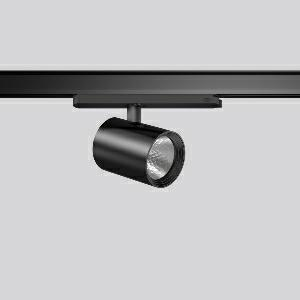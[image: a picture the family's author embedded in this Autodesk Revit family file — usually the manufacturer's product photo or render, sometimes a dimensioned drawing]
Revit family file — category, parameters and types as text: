
# Revit family: deecos_s_mini_track-in_742250_003_2_76_301b
name_source: partatom
category: Lighting Fixtures
units: mm (PartAtom-declared; Revit-internal decimal feet)

## family parameters
Cut with Voids When Loaded = No
Host = Face
Light Source = No
Part Type = Normal
Room Calculation Point = No
Round Connector Dimension = Use Diameter
Shared = No

## types (1)
- DEECOS S mini track-in (1 x LED Modul 927, 2400 lm, 2700)
    Apparent Load = 20 VA
    Approval mark = CE
    CIE Flux Codes = 100 100 100 100 100
    Color Rendering = 92
    Color Temperature = 2700
    Default Elevation = 1800 mm
    Description = Series: DEECOS S mini track-in
LED surface-mounted projector in modern design with no visible cooling ribs. Housing: die-cast aluminium, powder-coated. Rotation range: 356°. Swivel range: 90°. Black plastic ring and recessed LED to prevent glare from the side. Optical assembly with reflector made of MIRO-Silver with 98% total light reflection for outstanding efficiency - can be changed without tools. Best colour rendering index Ra>90. With adapter for RZB 3-circuit DALI tracks. Suitable for Track on ceiling, Wall track. Track-in driver integrated into the adapter. High quality converter without flickering and stroboscopic effect. The following accessories can be mounted without use of tools: interchangeable lenses, decorative glasses, honeycomb louvre, clear and frosted diffusers, white interchangeable plastic ring. 
Colour: deep black, matt (RAL 9005)
Diameter: 87 mm
Height: 135 mm
Lamp: LED
Socket: without socket
Colour temperature: 2700K
Colour rendering index (CRI): 92
System power: 20 W
Rated luminous flux: 2400 lm
Luminous efficiency: 120 lm/W
Control gear: Converter, dimmable, DALI
Protection class: II
Type of protection: IP 20
    Height = 135 mm
    Lamp = 1 x LED Modul 927
    Lamp Light Flux = 2400 lm
    Lamp count = 1
    Length = 87 mm
    Lifetime = 50000 h
    Luminous efficacy = 120 lm/W
    Manufacturer = RZB
    ModVariant = No
    Model = 742250.003.2.76
    Mounting Place = Ceiling
    Mounting Type = Rail mounted
    Number of Poles = 1
    OnlyDefault = Yes
    Power Factor = 1
    Product Name = DEECOS S mini track-in
    Product group = Track mounted projectors
    ProductGroupID = 301
    Protection Class = Protection class II
    Protection Degree = IP 20
    RLX_Detail_Level = 1
    RLX_Emergency_Light_Flux = 0 lm
    RLX_Emergency_Type = 0
    RLX_Emergency_Type_DB = No
    RlxData = <blob elided: 37401 chars, md5=6c86d3d4>
    Socket = socket
    Standby Power = 0 W
    System Light Flux = 2400 lm
    System Power = 20 W
    Type Comments = Product without accessories
    Type Image = 742105.003.jpg
    URL = http://relux.com
    VarID = ---
    Voltage = 230 V
    Voltage Range = 220-240 V
    Weight = 0.00 kg
    Width = 0 mm  [stored 0 ft]

note: [stored X ft] marks values corroborated as IEEE doubles in the binary element streams (Revit-internal decimal feet)

## geometry (parser evidence)
native form markers: Blend x4, Sweep x13
no freeform markers — native parametric forms only
